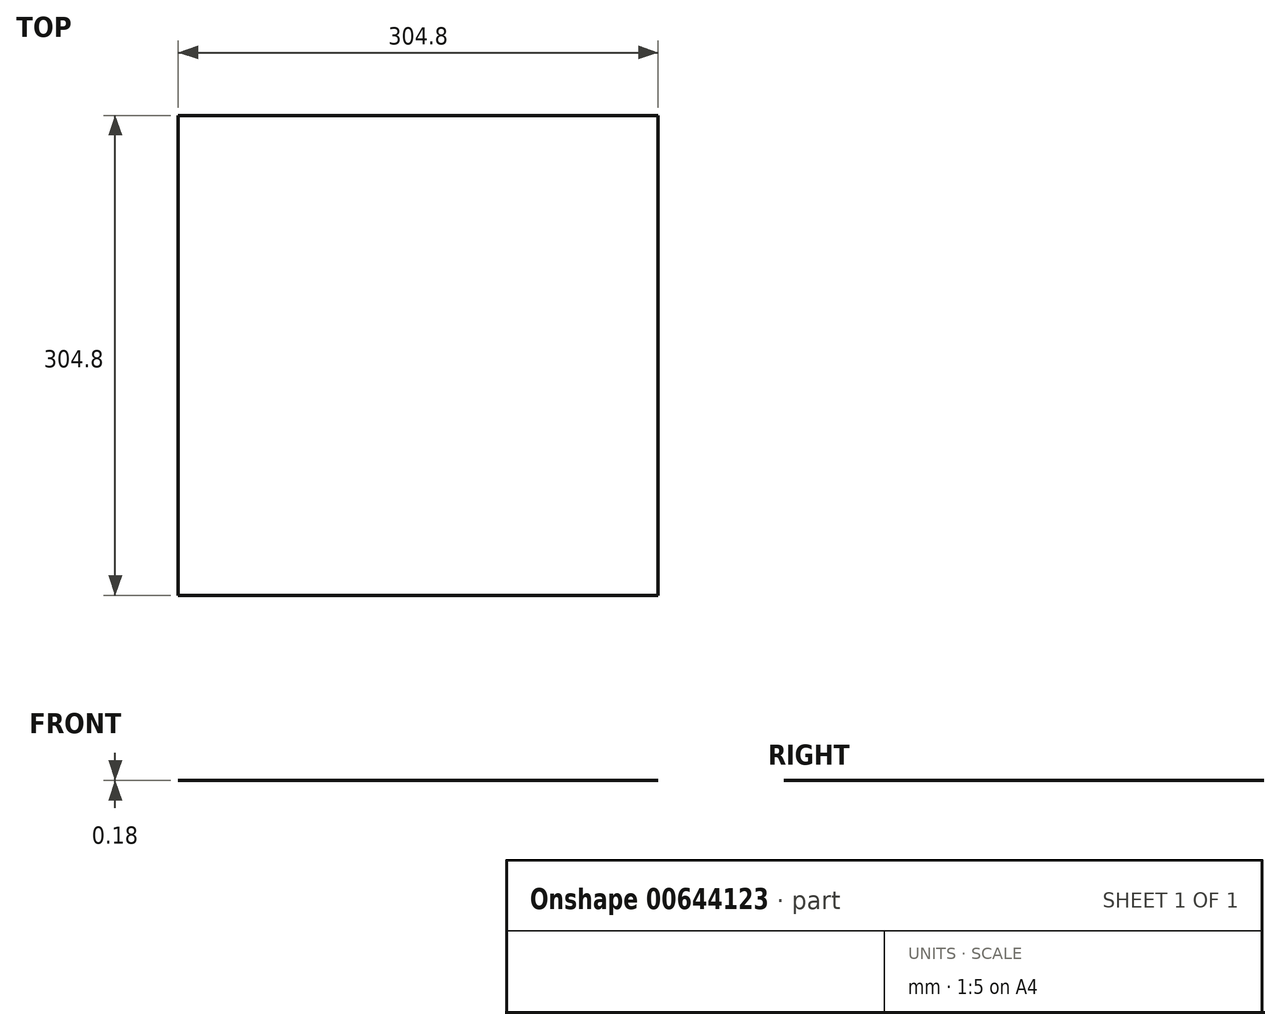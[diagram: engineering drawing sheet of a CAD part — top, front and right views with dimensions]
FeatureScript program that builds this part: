
annotation { "Feature Type Name" : "Feature", "Feature Type Description" : "" }
export const myFeature = defineFeature(function(context is Context, id is Id, definition is map)
    precondition{}
    {
        {
            var Q0;
            Q0=qCreatedBy(makeId("Top.planeOp"),FACE);
            var sketch = newSketch(context, id + "F0", { "sketchPlane" : qUnion([Q0])});
            skLineSegment(sketch, "E0.bottom", {"start": v(0, 0) * mm, "end": v(-304.8, 0) * mm});
            skLineSegment(sketch, "E0.top", {"start": v(0, 304.8) * mm, "end": v(-304.8, 304.8) * mm});
            skLineSegment(sketch, "E0.left", {"start": v(0, 0) * mm, "end": v(0, 304.8) * mm});
            skLineSegment(sketch, "E0.right", {"start": v(-304.8, 0) * mm, "end": v(-304.8, 304.8) * mm});
            skSolve(sketch);
        }
        {
            var Q0;
            Q0=makeQuery(id+"F0.imprint","IMPRINT",FACE,{"disambiguationData":[TD([[makeQuery(id+"F0.imprint","IMPRINT",EDGE,{"derivedFrom":sQuery(id+"F0.wireOp",EDGE,"E0.bottom")}),-1.0]])]});
            extrude(context, id + "F1", {"entities" : qUnion([Q0]), "depth" : 0.18 * mm, "offsetDistance" : 25.4 * mm});
        }
    });
